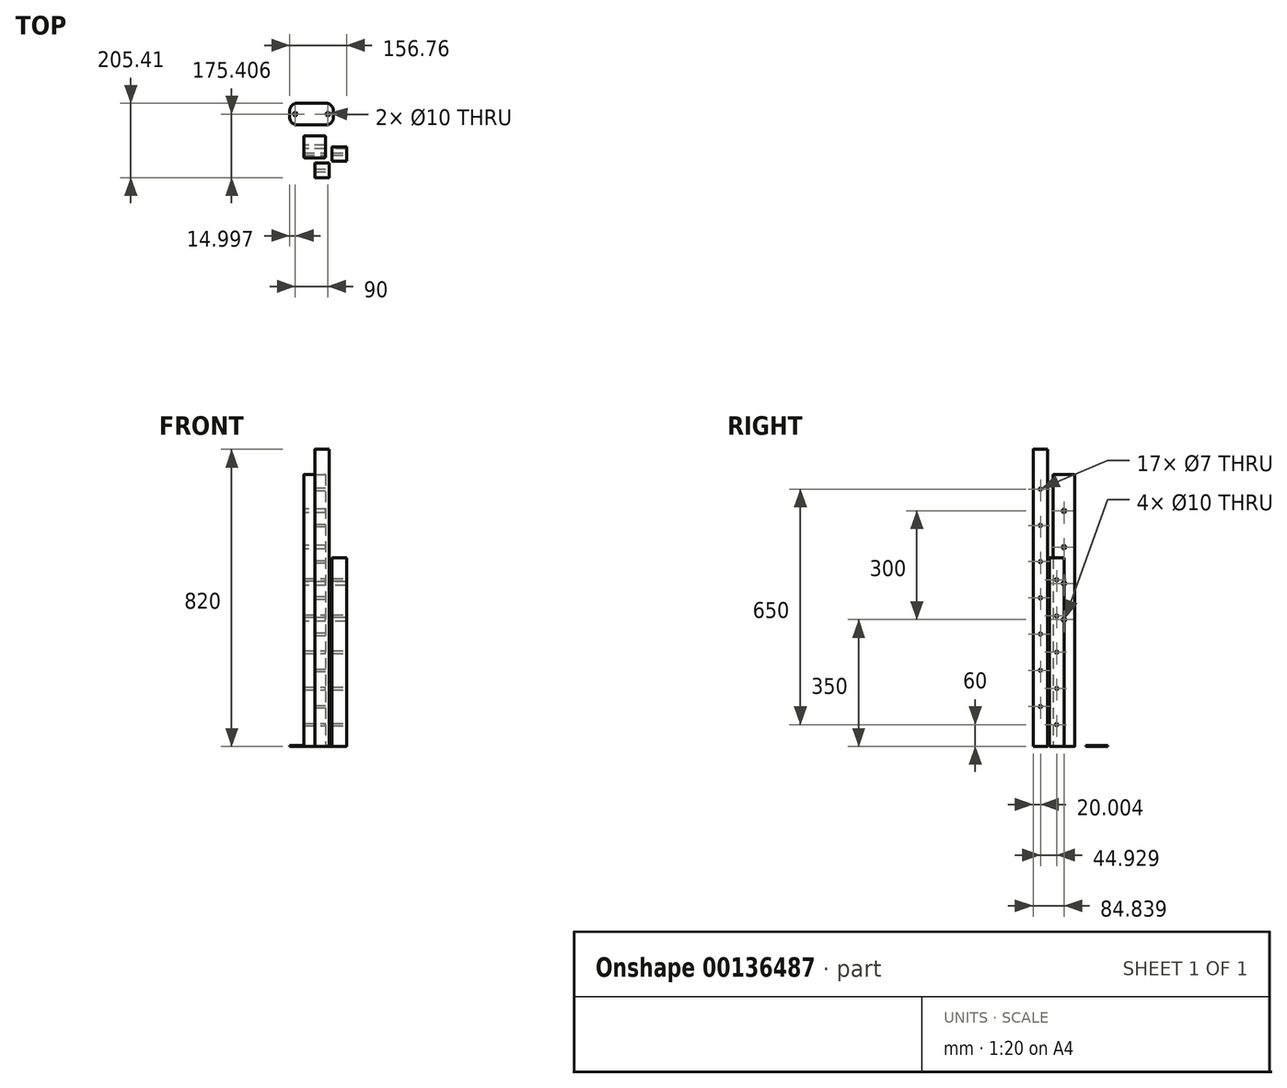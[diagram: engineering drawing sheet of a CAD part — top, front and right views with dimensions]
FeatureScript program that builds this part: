
annotation { "Feature Type Name" : "Feature", "Feature Type Description" : "" }
export const myFeature = defineFeature(function(context is Context, id is Id, definition is map)
    precondition{}
    {
        {
            var Q0;
            Q0=qCreatedBy(makeId("Top.planeOp"),FACE);
            var sketch = newSketch(context, id + "F0", { "sketchPlane" : qUnion([Q0])});
            skLineSegment(sketch, "E0.bottom", {"start": v(-110.98, 82.82) * mm, "end": v(-54.98, 82.82) * mm});
            skLineSegment(sketch, "E0.top", {"start": v(-110.98, 22.82) * mm, "end": v(-54.98, 22.82) * mm});
            skLineSegment(sketch, "E0.left", {"start": v(-112.98, 80.82) * mm, "end": v(-112.98, 24.82) * mm});
            skLineSegment(sketch, "E0.right", {"start": v(-52.98, 80.82) * mm, "end": v(-52.98, 24.82) * mm});
            skPoint(sketch, "E1.visualSharp", {"position": v(-112.98, 82.82) * mm});
            skArc(sketch, "E1.filletArc", {"start": v(-110.98, 82.82) * mm, "mid": v(-112.4, 82.23) * mm, "end": v(-112.98, 80.82) * mm});
            skPoint(sketch, "E2.visualSharp", {"position": v(-52.98, 82.82) * mm});
            skArc(sketch, "E2.filletArc", {"start": v(-52.98, 80.82) * mm, "mid": v(-53.57, 82.23) * mm, "end": v(-54.98, 82.82) * mm});
            skPoint(sketch, "E3.visualSharp", {"position": v(-52.98, 22.82) * mm});
            skArc(sketch, "E3.filletArc", {"start": v(-54.98, 22.82) * mm, "mid": v(-53.57, 23.4) * mm, "end": v(-52.98, 24.82) * mm});
            skPoint(sketch, "E4.visualSharp", {"position": v(-112.98, 22.82) * mm});
            skArc(sketch, "E4.filletArc", {"start": v(-112.98, 24.82) * mm, "mid": v(-112.4, 23.4) * mm, "end": v(-110.98, 22.82) * mm});
            skSolve(sketch);
        }
        {
            var Q0;
            Q0=makeQuery(id+"F0.imprint","IMPRINT",FACE,{"disambiguationData":[TD([[makeQuery(id+"F0.imprint","IMPRINT",EDGE,{"derivedFrom":sQuery(id+"F0.wireOp",EDGE,"E0.bottom")}),-1.0]])]});
            extrude(context, id + "F1", {"entities" : qUnion([Q0]), "depth" : 750 * mm});
        }
        {
            var Q0;
            Q0=qCreatedBy(makeId("Top.planeOp"),FACE);
            var sketch = newSketch(context, id + "F2", { "sketchPlane" : qUnion([Q0])});
            skLineSegment(sketch, "E5.bottom", {"start": v(-33.74, 52.91) * mm, "end": v(4.26, 52.91) * mm});
            skLineSegment(sketch, "E5.top", {"start": v(-33.74, 12.91) * mm, "end": v(4.26, 12.91) * mm});
            skLineSegment(sketch, "E5.left", {"start": v(-34.74, 51.91) * mm, "end": v(-34.74, 13.91) * mm});
            skLineSegment(sketch, "E5.right", {"start": v(5.26, 51.91) * mm, "end": v(5.26, 13.91) * mm});
            skPoint(sketch, "E6.visualSharp", {"position": v(-34.74, 52.91) * mm});
            skArc(sketch, "E6.filletArc", {"start": v(-33.74, 52.91) * mm, "mid": v(-34.45, 52.62) * mm, "end": v(-34.74, 51.91) * mm});
            skPoint(sketch, "E7.visualSharp", {"position": v(5.26, 52.91) * mm});
            skArc(sketch, "E7.filletArc", {"start": v(5.26, 51.91) * mm, "mid": v(4.97, 52.62) * mm, "end": v(4.26, 52.91) * mm});
            skPoint(sketch, "E8.visualSharp", {"position": v(-34.74, 12.91) * mm});
            skArc(sketch, "E8.filletArc", {"start": v(-34.74, 13.91) * mm, "mid": v(-34.45, 13.2) * mm, "end": v(-33.74, 12.91) * mm});
            skPoint(sketch, "E9.visualSharp", {"position": v(5.26, 12.91) * mm});
            skArc(sketch, "E9.filletArc", {"start": v(4.26, 12.91) * mm, "mid": v(4.97, 13.2) * mm, "end": v(5.26, 13.91) * mm});
            skSolve(sketch);
        }
        {
            var Q0;
            Q0=makeQuery(id+"F2.imprint","IMPRINT",FACE,{"disambiguationData":[TD([[makeQuery(id+"F2.imprint","IMPRINT",EDGE,{"derivedFrom":sQuery(id+"F2.wireOp",EDGE,"E5.bottom")}),-1.0]])]});
            extrude(context, id + "F3", {"entities" : qUnion([Q0]), "depth" : 520 * mm});
        }
        {
            var Q0;
            Q0=qCreatedBy(makeId("Top.planeOp"),FACE);
            var sketch = newSketch(context, id + "F4", { "sketchPlane" : qUnion([Q0])});
            skLineSegment(sketch, "E10.bottom", {"start": v(-81.76, 7.98) * mm, "end": v(-43.76, 7.98) * mm});
            skLineSegment(sketch, "E10.top", {"start": v(-81.76, -32.02) * mm, "end": v(-43.76, -32.02) * mm});
            skLineSegment(sketch, "E10.left", {"start": v(-82.76, 6.98) * mm, "end": v(-82.76, -31.02) * mm});
            skLineSegment(sketch, "E10.right", {"start": v(-42.76, 6.98) * mm, "end": v(-42.76, -31.02) * mm});
            skPoint(sketch, "E11.visualSharp", {"position": v(-82.76, 7.98) * mm});
            skArc(sketch, "E11.filletArc", {"start": v(-81.76, 7.98) * mm, "mid": v(-82.47, 7.7) * mm, "end": v(-82.76, 6.98) * mm});
            skPoint(sketch, "E12.visualSharp", {"position": v(-42.76, 7.98) * mm});
            skArc(sketch, "E12.filletArc", {"start": v(-42.76, 6.98) * mm, "mid": v(-43.05, 7.7) * mm, "end": v(-43.76, 7.98) * mm});
            skPoint(sketch, "E13.visualSharp", {"position": v(-42.76, -32.02) * mm});
            skArc(sketch, "E13.filletArc", {"start": v(-43.76, -32.02) * mm, "mid": v(-43.05, -31.72) * mm, "end": v(-42.76, -31.02) * mm});
            skPoint(sketch, "E14.visualSharp", {"position": v(-82.76, -32.02) * mm});
            skArc(sketch, "E14.filletArc", {"start": v(-82.76, -31.02) * mm, "mid": v(-82.47, -31.72) * mm, "end": v(-81.76, -32.02) * mm});
            skSolve(sketch);
        }
        {
            var Q0;
            Q0=makeQuery(id+"F4.imprint","IMPRINT",FACE,{"disambiguationData":[TD([[makeQuery(id+"F4.imprint","IMPRINT",EDGE,{"derivedFrom":sQuery(id+"F4.wireOp",EDGE,"E10.bottom")}),-1.0]])]});
            extrude(context, id + "F5", {"entities" : qUnion([Q0]), "depth" : 820 * mm});
        }
        {
            var Q0;
            Q0=makeQuery(id+"F1.opExtrude","SWEPT_FACE",FACE,{"disambiguationData":[OSD([sQuery(id+"F0.wireOp",EDGE,"E0.left")])]});
            var sketch = newSketch(context, id + "F6", { "sketchPlane" : qUnion([Q0])});
            skLineSegment(sketch, "E15", {"start": v(-52.82, 750) * mm, "end": v(-52.82, 0) * mm, "construction": true});
            skCircle(sketch, "E16", {"center": v(-52.82, 650) * mm, "radius": 5 * mm});
            skCircle(sketch, "E17.0.1.0", {"center": v(-52.82, 550) * mm, "radius": 5 * mm});
            skCircle(sketch, "E17.0.2.0", {"center": v(-52.82, 450) * mm, "radius": 5 * mm});
            skCircle(sketch, "E17.0.3.0", {"center": v(-52.82, 350) * mm, "radius": 5 * mm});
            skLineSegment(sketch, "E17.direction1", {"start": v(-52.82, 650) * mm, "end": v(-11.75, 659.79) * mm, "construction": true});
            skLineSegment(sketch, "E17.direction2", {"start": v(-52.82, 650) * mm, "end": v(-52.82, 550) * mm, "construction": true});
            skSolve(sketch);
        }
        {
            var Q0;
            Q0=makeQuery(id+"F6.imprint","IMPRINT",FACE,{"disambiguationData":[TD([[makeQuery(id+"F6.imprint","IMPRINT",EDGE,{"derivedFrom":sQuery(id+"F6.wireOp",EDGE,"E16")}),1.0]])]});
            var Q1;
            Q1=makeQuery(id+"F6.imprint","IMPRINT",FACE,{"disambiguationData":[TD([[makeQuery(id+"F6.imprint","IMPRINT",EDGE,{"derivedFrom":sQuery(id+"F6.wireOp",EDGE,"E17.0.1.0")}),1.0]])]});
            var Q2;
            Q2=makeQuery(id+"F6.imprint","IMPRINT",FACE,{"disambiguationData":[TD([[makeQuery(id+"F6.imprint","IMPRINT",EDGE,{"derivedFrom":sQuery(id+"F6.wireOp",EDGE,"E17.0.2.0")}),1.0]])]});
            var Q3;
            Q3=makeQuery(id+"F6.imprint","IMPRINT",FACE,{"disambiguationData":[TD([[makeQuery(id+"F6.imprint","IMPRINT",EDGE,{"derivedFrom":sQuery(id+"F6.wireOp",EDGE,"E17.0.3.0")}),1.0]])]});
            extrude(context, id + "F7", {"entities" : qUnion([Q0, Q1, Q2, Q3]), "operationType" : NewBodyOperationType.REMOVE, "endBound" : BoundingType.THROUGH_ALL, "oppositeDirection" : true, "depth" : 25 * mm});
        }
        {
            var Q0;
            Q0=qCreatedBy(makeId("Top.planeOp"),FACE);
            var sketch = newSketch(context, id + "F8", { "sketchPlane" : qUnion([Q0])});
            skLineSegment(sketch, "E18.bottom", {"start": v(-131.5, 173.39) * mm, "end": v(-51.5, 173.39) * mm});
            skLineSegment(sketch, "E18.top", {"start": v(-131.5, 113.39) * mm, "end": v(-51.5, 113.39) * mm});
            skLineSegment(sketch, "E18.left", {"start": v(-151.5, 153.39) * mm, "end": v(-151.5, 133.39) * mm});
            skLineSegment(sketch, "E18.right", {"start": v(-31.5, 153.39) * mm, "end": v(-31.5, 133.39) * mm});
            skPoint(sketch, "E19.visualSharp", {"position": v(-151.5, 173.39) * mm});
            skArc(sketch, "E19.filletArc", {"start": v(-131.5, 173.39) * mm, "mid": v(-145.64, 167.53) * mm, "end": v(-151.5, 153.39) * mm});
            skPoint(sketch, "E20.visualSharp", {"position": v(-151.5, 113.39) * mm});
            skArc(sketch, "E20.filletArc", {"start": v(-151.5, 133.39) * mm, "mid": v(-145.64, 119.24) * mm, "end": v(-131.5, 113.39) * mm});
            skPoint(sketch, "E21.visualSharp", {"position": v(-31.5, 113.39) * mm});
            skArc(sketch, "E21.filletArc", {"start": v(-51.5, 113.39) * mm, "mid": v(-37.36, 119.24) * mm, "end": v(-31.5, 133.39) * mm});
            skPoint(sketch, "E22.visualSharp", {"position": v(-31.5, 173.39) * mm});
            skArc(sketch, "E22.filletArc", {"start": v(-31.5, 153.39) * mm, "mid": v(-37.36, 167.53) * mm, "end": v(-51.5, 173.39) * mm});
            skLineSegment(sketch, "E23", {"start": v(-151.5, 143.39) * mm, "end": v(-31.5, 143.39) * mm, "construction": true});
            skLineSegment(sketch, "E24", {"start": v(-91.5, 173.39) * mm, "end": v(-91.5, 113.39) * mm, "construction": true});
            skCircle(sketch, "E25", {"center": v(-136.5, 143.39) * mm, "radius": 5 * mm});
            skCircle(sketch, "E26", {"center": v(-46.5, 143.39) * mm, "radius": 5 * mm});
            skSolve(sketch);
        }
        {
            var Q0;
            Q0=makeQuery(id+"F8.imprint","IMPRINT",FACE,{"disambiguationData":[TD([[makeQuery(id+"F8.imprint","IMPRINT",EDGE,{"derivedFrom":sQuery(id+"F8.wireOp",EDGE,"E18.bottom")}),-1.0]])]});
            extrude(context, id + "F9", {"entities" : qUnion([Q0]), "depth" : 3 * mm});
        }
        {
            var Q0;
            Q0=makeQuery(id+"F5.opExtrude","SWEPT_FACE",FACE,{"disambiguationData":[OSD([sQuery(id+"F4.wireOp",EDGE,"E10.right")])]});
            var sketch = newSketch(context, id + "F10", { "sketchPlane" : qUnion([Q0])});
            skLineSegment(sketch, "E27", {"start": v(-12.02, 820) * mm, "end": v(-12.02, 0) * mm, "construction": true});
            skCircle(sketch, "E28", {"center": v(-12.02, 410) * mm, "radius": 3.5 * mm});
            skCircle(sketch, "E29.0.1.0", {"center": v(-12.02, 510) * mm, "radius": 3.5 * mm});
            skCircle(sketch, "E29.0.2.0", {"center": v(-12.02, 610) * mm, "radius": 3.5 * mm});
            skCircle(sketch, "E29.0.3.0", {"center": v(-12.02, 710) * mm, "radius": 3.5 * mm});
            skLineSegment(sketch, "E29.direction1", {"start": v(-12.02, 410) * mm, "end": v(17.98, 410) * mm, "construction": true});
            skLineSegment(sketch, "E29.direction2", {"start": v(-12.02, 410) * mm, "end": v(-12.02, 510) * mm, "construction": true});
            skCircle(sketch, "E30.0.1.0", {"center": v(-12.02, 310) * mm, "radius": 3.5 * mm});
            skCircle(sketch, "E30.0.2.0", {"center": v(-12.02, 210) * mm, "radius": 3.5 * mm});
            skCircle(sketch, "E30.0.3.0", {"center": v(-12.02, 110) * mm, "radius": 3.5 * mm});
            skLineSegment(sketch, "E30.direction2", {"start": v(-12.02, 410) * mm, "end": v(-12.02, 310) * mm, "construction": true});
            skSolve(sketch);
        }
        {
            var Q0;
            Q0=makeQuery(id+"F10.imprint","IMPRINT",FACE,{"disambiguationData":[TD([[makeQuery(id+"F10.imprint","IMPRINT",EDGE,{"derivedFrom":sQuery(id+"F10.wireOp",EDGE,"E28")}),1.0]])]});
            var Q1;
            Q1=makeQuery(id+"F10.imprint","IMPRINT",FACE,{"disambiguationData":[TD([[makeQuery(id+"F10.imprint","IMPRINT",EDGE,{"derivedFrom":sQuery(id+"F10.wireOp",EDGE,"E29.0.1.0")}),1.0]])]});
            var Q2;
            Q2=makeQuery(id+"F10.imprint","IMPRINT",FACE,{"disambiguationData":[TD([[makeQuery(id+"F10.imprint","IMPRINT",EDGE,{"derivedFrom":sQuery(id+"F10.wireOp",EDGE,"E29.0.2.0")}),1.0]])]});
            var Q3;
            Q3=makeQuery(id+"F10.imprint","IMPRINT",FACE,{"disambiguationData":[TD([[makeQuery(id+"F10.imprint","IMPRINT",EDGE,{"derivedFrom":sQuery(id+"F10.wireOp",EDGE,"E29.0.3.0")}),1.0]])]});
            var Q4;
            Q4=makeQuery(id+"F10.imprint","IMPRINT",FACE,{"disambiguationData":[TD([[makeQuery(id+"F10.imprint","IMPRINT",EDGE,{"derivedFrom":sQuery(id+"F10.wireOp",EDGE,"E30.0.1.0")}),1.0]])]});
            var Q5;
            Q5=makeQuery(id+"F10.imprint","IMPRINT",FACE,{"disambiguationData":[TD([[makeQuery(id+"F10.imprint","IMPRINT",EDGE,{"derivedFrom":sQuery(id+"F10.wireOp",EDGE,"E30.0.2.0")}),1.0]])]});
            var Q6;
            Q6=makeQuery(id+"F10.imprint","IMPRINT",FACE,{"disambiguationData":[TD([[makeQuery(id+"F10.imprint","IMPRINT",EDGE,{"derivedFrom":sQuery(id+"F10.wireOp",EDGE,"E30.0.3.0")}),1.0]])]});
            extrude(context, id + "F11", {"entities" : qUnion([Q0, Q1, Q2, Q3, Q4, Q5, Q6]), "operationType" : NewBodyOperationType.REMOVE, "endBound" : BoundingType.THROUGH_ALL, "oppositeDirection" : true, "depth" : 25 * mm});
        }
        {
            var Q0;
            Q0=makeQuery(id+"F3.opExtrude","SWEPT_FACE",FACE,{"disambiguationData":[OSD([sQuery(id+"F2.wireOp",EDGE,"E5.right")])]});
            var sketch = newSketch(context, id + "F12", { "sketchPlane" : qUnion([Q0])});
            skLineSegment(sketch, "E31", {"start": v(32.91, 520) * mm, "end": v(32.91, 0) * mm, "construction": true});
            skCircle(sketch, "E32", {"center": v(32.91, 260) * mm, "radius": 3.5 * mm});
            skCircle(sketch, "E33.0.1.0", {"center": v(32.91, 360) * mm, "radius": 3.5 * mm});
            skCircle(sketch, "E33.0.2.0", {"center": v(32.91, 460) * mm, "radius": 3.5 * mm});
            skLineSegment(sketch, "E33.direction1", {"start": v(32.91, 260) * mm, "end": v(52.91, 260) * mm, "construction": true});
            skLineSegment(sketch, "E33.direction2", {"start": v(32.91, 260) * mm, "end": v(32.91, 360) * mm, "construction": true});
            skCircle(sketch, "E34.0.1.0", {"center": v(32.91, 160) * mm, "radius": 3.5 * mm});
            skCircle(sketch, "E34.0.2.0", {"center": v(32.91, 60) * mm, "radius": 3.5 * mm});
            skLineSegment(sketch, "E34.direction2", {"start": v(32.91, 260) * mm, "end": v(32.91, 160) * mm, "construction": true});
            skSolve(sketch);
        }
        {
            var Q0;
            Q0=makeQuery(id+"F12.imprint","IMPRINT",FACE,{"disambiguationData":[TD([[makeQuery(id+"F12.imprint","IMPRINT",EDGE,{"derivedFrom":sQuery(id+"F12.wireOp",EDGE,"E32")}),1.0]])]});
            var Q1;
            Q1=makeQuery(id+"F12.imprint","IMPRINT",FACE,{"disambiguationData":[TD([[makeQuery(id+"F12.imprint","IMPRINT",EDGE,{"derivedFrom":sQuery(id+"F12.wireOp",EDGE,"E33.0.1.0")}),1.0]])]});
            var Q2;
            Q2=makeQuery(id+"F12.imprint","IMPRINT",FACE,{"disambiguationData":[TD([[makeQuery(id+"F12.imprint","IMPRINT",EDGE,{"derivedFrom":sQuery(id+"F12.wireOp",EDGE,"E33.0.2.0")}),1.0]])]});
            var Q3;
            Q3=makeQuery(id+"F12.imprint","IMPRINT",FACE,{"disambiguationData":[TD([[makeQuery(id+"F12.imprint","IMPRINT",EDGE,{"derivedFrom":sQuery(id+"F12.wireOp",EDGE,"E34.0.1.0")}),1.0]])]});
            var Q4;
            Q4=makeQuery(id+"F12.imprint","IMPRINT",FACE,{"disambiguationData":[TD([[makeQuery(id+"F12.imprint","IMPRINT",EDGE,{"derivedFrom":sQuery(id+"F12.wireOp",EDGE,"E34.0.2.0")}),1.0]])]});
            extrude(context, id + "F13", {"entities" : qUnion([Q0, Q1, Q2, Q3, Q4]), "operationType" : NewBodyOperationType.REMOVE, "endBound" : BoundingType.THROUGH_ALL, "oppositeDirection" : true, "depth" : 25 * mm});
        }
    });
